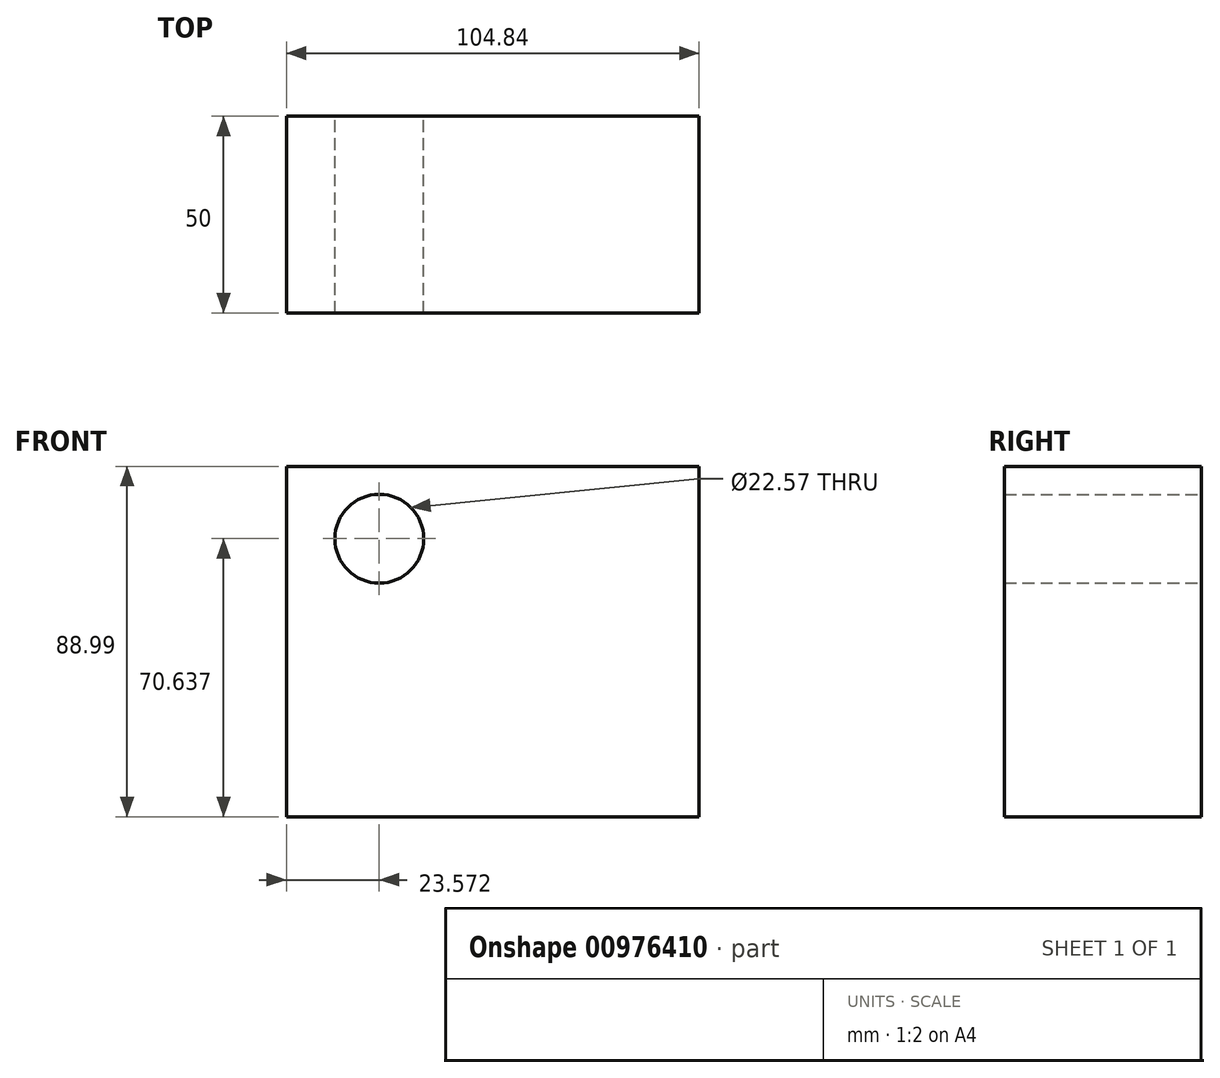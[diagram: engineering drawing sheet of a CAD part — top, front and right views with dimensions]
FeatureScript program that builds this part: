
annotation { "Feature Type Name" : "Feature", "Feature Type Description" : "" }
export const myFeature = defineFeature(function(context is Context, id is Id, definition is map)
    precondition{}
    {
        {
            var Q0;
            Q0=qCreatedBy(makeId("Front.planeOp"),FACE);
            var sketch = newSketch(context, id + "F0", { "sketchPlane" : qUnion([Q0])});
            skLineSegment(sketch, "E0.bottom", {"start": v(-52.42, 36.93) * mm, "end": v(52.42, 36.93) * mm});
            skLineSegment(sketch, "E0.top", {"start": v(-52.42, -52.06) * mm, "end": v(52.42, -52.06) * mm});
            skLineSegment(sketch, "E0.left", {"start": v(-52.42, 36.93) * mm, "end": v(-52.42, -52.06) * mm});
            skLineSegment(sketch, "E0.right", {"start": v(52.42, 36.93) * mm, "end": v(52.42, -52.06) * mm});
            skLineSegment(sketch, "E1.bottom", {"start": v(-12.43, 36.93) * mm, "end": v(-12.43, 36.93) * mm});
            skCircle(sketch, "E2", {"center": v(-28.85, 18.58) * mm, "radius": 11.29 * mm});
            skSolve(sketch);
        }
        {
            var Q0;
            Q0 = qSketchRegion(id + "F0", true);
            extrude(context, id + "F1", {"entities" : qUnion([Q0]), "depth" : 50 * mm, "offsetDistance" : 25 * mm});
        }
        {
            var Q0;
            Q0=makeQuery(id+"F0.imprint","IMPRINT",FACE,{"disambiguationData":[TD([[makeQuery(id+"F0.imprint","IMPRINT",EDGE,{"derivedFrom":sQuery(id+"F0.wireOp",EDGE,"E2")}),1.0]])]});
            extrude(context, id + "F2", {"entities" : qUnion([Q0]), "operationType" : NewBodyOperationType.REMOVE, "oppositeDirection" : true, "depth" : 25 * mm, "offsetDistance" : 25 * mm});
        }
    });
